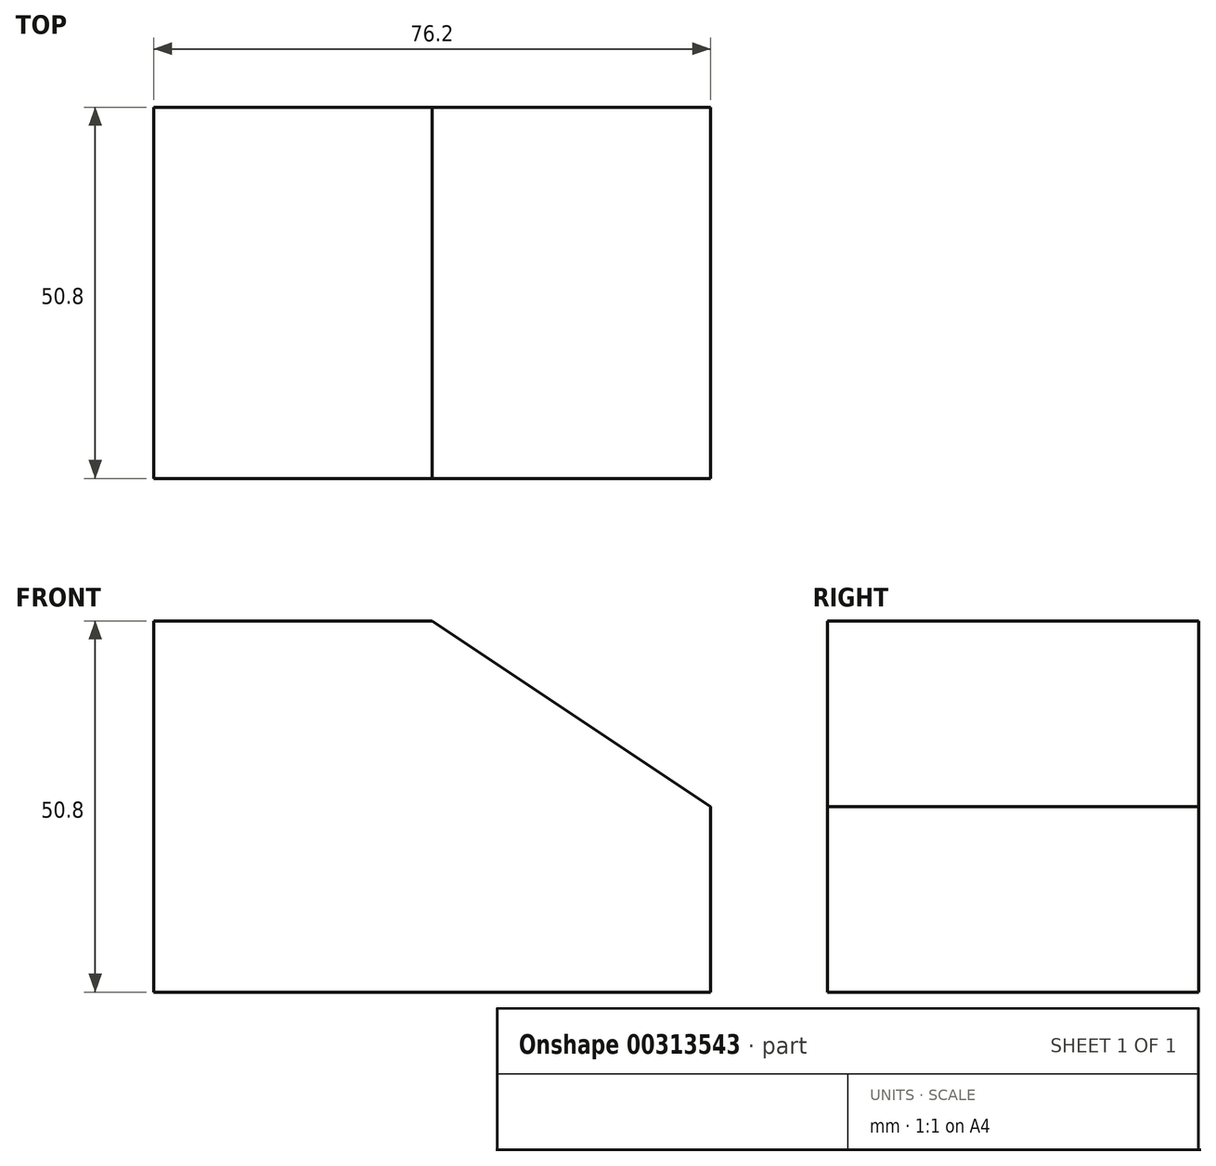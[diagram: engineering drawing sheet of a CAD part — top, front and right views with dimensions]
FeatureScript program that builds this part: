
annotation { "Feature Type Name" : "Feature", "Feature Type Description" : "" }
export const myFeature = defineFeature(function(context is Context, id is Id, definition is map)
    precondition{}
    {
        {
            var Q0;
            Q0=qCreatedBy(makeId("Front.planeOp"),FACE);
            var sketch = newSketch(context, id + "F0", { "sketchPlane" : qUnion([Q0])});
            skLineSegment(sketch, "E0", {"start": v(-42.86, -42.23) * mm, "end": v(33.34, -42.23) * mm});
            skLineSegment(sketch, "E1", {"start": v(33.34, -42.23) * mm, "end": v(33.34, -16.83) * mm});
            skLineSegment(sketch, "E2", {"start": v(33.34, -16.83) * mm, "end": v(-4.76, 8.57) * mm});
            skLineSegment(sketch, "E3", {"start": v(-4.76, 8.57) * mm, "end": v(-42.86, 8.57) * mm});
            skLineSegment(sketch, "E4", {"start": v(-42.86, 8.57) * mm, "end": v(-42.86, -42.23) * mm});
            skSolve(sketch);
        }
        {
            var Q0;
            Q0 = qSketchRegion(id + "F0", true);
            extrude(context, id + "F1", {"entities" : qUnion([Q0]), "depth" : 50.8 * mm});
        }
    });
